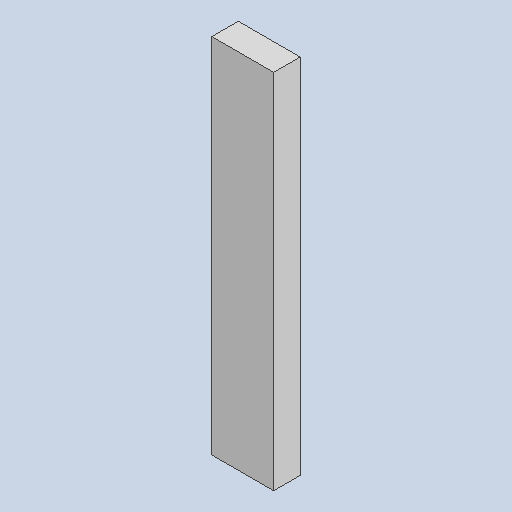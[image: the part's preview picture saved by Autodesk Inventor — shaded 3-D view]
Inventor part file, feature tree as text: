
AUTODESK INVENTOR PART (.ipt)
format: ipt  version: 2025 (Build 290162000, 162)  size: 134,144 bytes
history: native  units: in
note: dims shown in document units (in); Inventor stores cm internally (conversion verified against a paired STEP export)
features: other x4, reference x3, extrude x1, sketch x1
ambient origin geometry x8: Origin, YZ Plane, XZ Plane, XY Plane, X Axis, Y Axis, Z Axis, Center Point
bodies: Solid1 (feature_tree)
feature tree (9):
  extrude  "Extrusion1"  Depth=1.5in TaperAngle=0.0deg
  sketch  "Sketch1"  dims[d0=3.5in d1=1.5in d2=0.0in]
  reference  "Reference1"
  reference  "Reference2"
  reference  "Reference3"
  other  "<userpath>\Documents\Tburn24\F_Legs2\F_Legs2.iam"
  other  "F_Legs2.iam"
  other  "side-side1:1"
  other  "8'x2x4:4"
